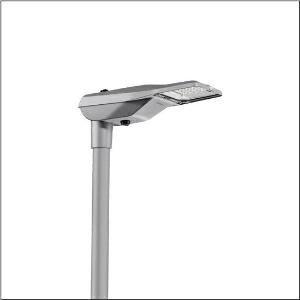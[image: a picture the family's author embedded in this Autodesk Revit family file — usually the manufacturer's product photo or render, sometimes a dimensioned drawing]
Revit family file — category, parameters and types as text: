
# Revit family: streetlight_sl_21_micro___st0_8a_5xe1c43t08db_13be
name_source: partatom
category: Lighting Fixtures
units: mm (PartAtom-declared; Revit-internal decimal feet)

## family parameters
Cut with Voids When Loaded = No
Host = Face
Light Source = No
Part Type = Normal
Room Calculation Point = No
Round Connector Dimension = Use Diameter
Shared = No

## types (1)
- --- (1 x LED, 5320 lm, 39.1 W, 4000K)
    Apparent Load = 39 VA
    CIE Flux Codes = 38 75 97 100 100
    Color Rendering = 70
    Color Temperature = 4000K
    Default Elevation = 1800 mm
    Description = Streetlight SL 21 micro, mast luminaire, primary light control with lens, of PMMA, primary optical cover: cover, of toughened safety glass, transparent, light distribution: ST0.8a, light emission: direct distribution, primary light characteristic: asymmetric, installation type: side-entry, post-top, LED, High Power LED, rated luminous flux: 5.320lm, luminous efficacy: 136lm/W, light colour: 740, colour temperature: 4000K, control: flexible luminous flux parameterisation, time-dependent luminous flux control, constant luminous flux control, overheat protection, pre-setting: logarithmic dimming characteristic, mains connection: 220..240V, AC, 50/60Hz, start of lifetime: 39W, end of service life: 41W, reduction: 18W, luminaire housing, of diecast aluminium, powder-coated, Siteco® metallic grey (DB 702S), corrosivity category C5 mid according to DIN EN ISO 12944, please order mast flange separately, inclination adjustable: 0°, 5°, 10°, 15°, sealing non-destructively replaceable, multi-level sealing system, length: 528mm, width: 235mm, height: 110mm, mast flange for spigot size: 42mm (side-entry): 5XC10008XM4, 60/48mm (side-entry/post-top): 5XC10108XM2, 76/60mm (side-entry/post-top): 5XC10108XM1, Smart Interface below and above, protection rating (complete): IP66, insulation class (complete): insulation class II (safety insulation), certification: CE, ENEC, ENEC+, VDE, impact resistance: IK09, permissible operating ambient temperature for outdoor applications: -40..+50°C, standard-compliant lighting for roads and squares, packaging unit: 1 piece

Light Distribution: ST0.8a
    Height = 110 mm
    Lamp = 1 x LED
    Lamp Light Flux = 5320 lm
    Lamp Power = 39.1 W
    Lamp count = 1
    Length = 528 mm
    Luminous efficacy = 136 lm/W
    Manufacturer = Siteco
    ModVariant = No
    Model = 5XE1C43T08DB
    Number of Poles = 1
    OnlyDefault = Yes
    Power Factor = 1
    Product Name = Streetlight SL 21 micro | ST0.8a
    Product group = mast luminaire | pylon top
    ProductGroupID = 6100
    Protection Class = Protection class II
    Protection Degree = IP 66
    RLX_Detail_Level = 1
    RLX_Emergency_Light_Flux = 0 lm
    RLX_Emergency_Type = 0
    RLX_Emergency_Type_DB = No
    RlxData = <blob elided: 98825 chars, md5=db9ce7df>
    Socket = socket
    Standby Power = 0 W
    System Light Flux = 5320 lm
    System Power = 39 W
    Type Comments = factory setting: luminous flux: 100 % | dim-lin: 254 | 765 mA
    Type Image = l_1007239.jpg
    URL = http://relux.com
    VarID = @adj_124685
    Voltage = 0 V
    Weight = 0.00 kg
    Width = 235 mm

## geometry (parser evidence)
native form markers: Blend x4, Sweep x11
no freeform markers — native parametric forms only
